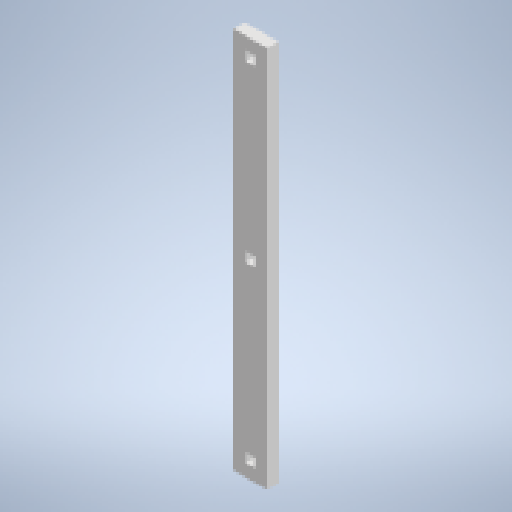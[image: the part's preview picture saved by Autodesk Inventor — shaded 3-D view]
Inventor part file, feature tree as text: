
AUTODESK INVENTOR PART (.ipt)
format: ipt  version: 2024 (Build 280153000, 153)  size: 193,536 bytes
history: native  units: in
note: dims shown in document units (in); Inventor stores cm internally (conversion verified against a paired STEP export)
features: extrude x2, sketch x1, pattern_linear x1, chamfer x1
ambient origin geometry x8: Origin, YZ Plane, XZ Plane, XY Plane, X Axis, Y Axis, Z Axis, Center Point
bodies: Solid1 (feature_tree)
feature tree (5):
  sketch  "Sketch1"  dims[d0=0.1614in d1=0.1614in d2=0.0807in d3=0.0807in d4=6.6929in d5=0.5906in d6=0.2953in d7=3.3465in d8=0.1969in d9=0.0in d10=0.1614in d11=0.0in d12=1.1811in d14=3.0457in d15=0.0197in d16=0.0787in d17=45.0deg d18=1.9685in d19=0.9843in d20=0.3937in]
  extrude  "Extrusion1"  Depth=0.1614in
  extrude  "Extrusion2"  Depth=0.3937in
  pattern_linear  "Rectangular Pattern1"  Spacing1=0.0807in  [1 undecoded]
  chamfer  "Chamfer1"  Distance=6.6929in
note: 1 required parameter value undecoded (feature->parameter linkage not recoverable at this tier; creation-order binding heuristic only, values carry confidence <= 0.55)
